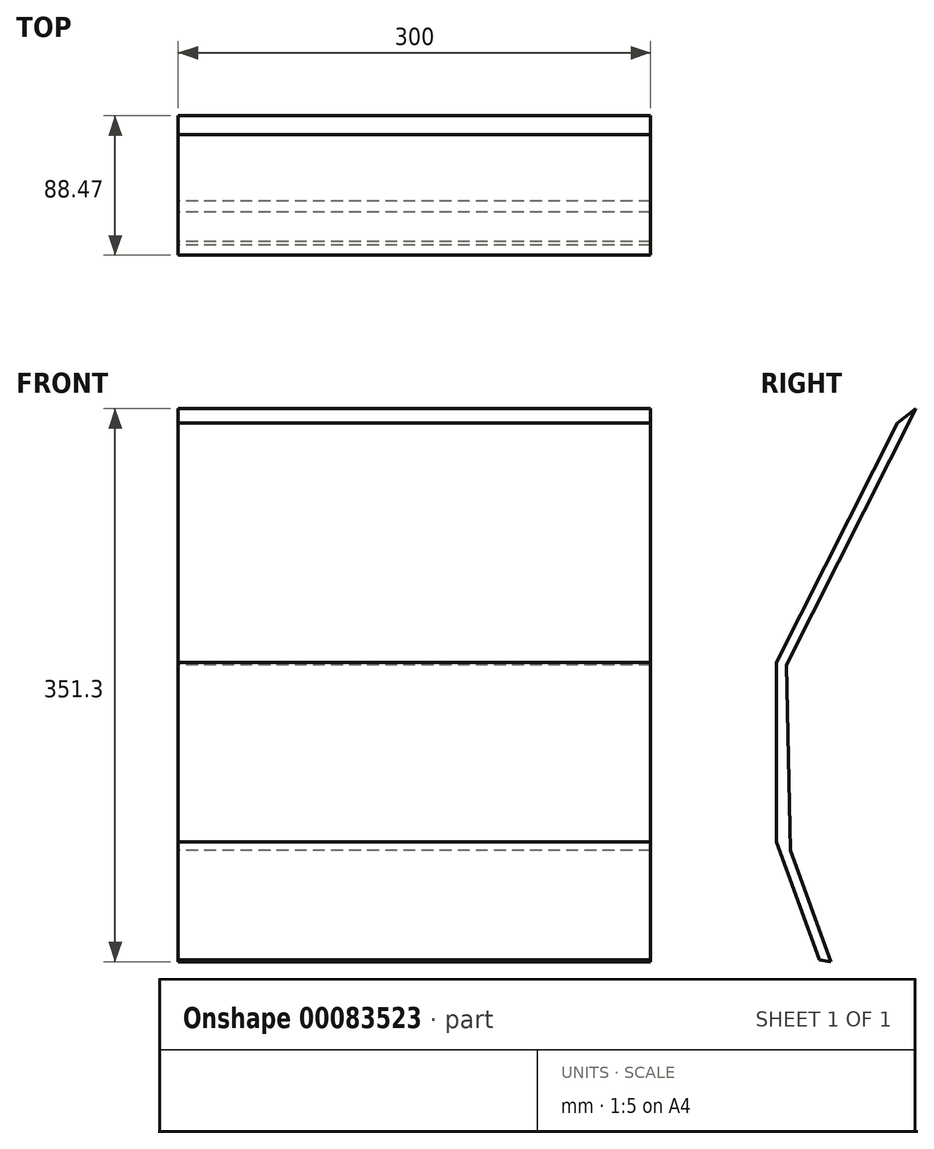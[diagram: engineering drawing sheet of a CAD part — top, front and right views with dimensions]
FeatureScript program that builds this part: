
annotation { "Feature Type Name" : "Feature", "Feature Type Description" : "" }
export const myFeature = defineFeature(function(context is Context, id is Id, definition is map)
    precondition{}
    {
        {
            var Q0;
            Q0=qCreatedBy(makeId("Right.planeOp"),FACE);
            var sketch = newSketch(context, id + "F0", { "sketchPlane" : qUnion([Q0])});
            skLineSegment(sketch, "E0", {"start": v(82.12, 328.82) * mm, "end": v(0, 165.98) * mm});
            skLineSegment(sketch, "E1.0", {"start": v(-6.35, 53.47) * mm, "end": v(20.89, -21.18) * mm});
            skLineSegment(sketch, "E1.1", {"start": v(-6.35, 167.5) * mm, "end": v(-6.35, 53.47) * mm});
            skLineSegment(sketch, "E1.2", {"start": v(70.34, 319.57) * mm, "end": v(-6.35, 167.5) * mm});
            skLineSegment(sketch, "E2", {"start": v(82.12, 328.82) * mm, "end": v(70.34, 319.57) * mm});
            skLineSegment(sketch, "E3", {"start": v(28.12, -22.48) * mm, "end": v(20.89, -21.18) * mm});
            skLineSegment(sketch, "E4.0", {"start": v(2.36, 48.14) * mm, "end": v(28.12, -22.48) * mm});
            skLineSegment(sketch, "E5", {"start": v(0, 165.98) * mm, "end": v(2.36, 48.14) * mm});
            skSolve(sketch);
        }
        {
            var Q0;
            Q0 = qSketchRegion(id + "F0", true);
            extrude(context, id + "F1", {"entities" : qUnion([Q0]), "depth" : 150 * mm, "hasSecondDirection" : true, "secondDirectionOppositeDirection" : true, "secondDirectionDepth" : 150 * mm});
        }
    });
